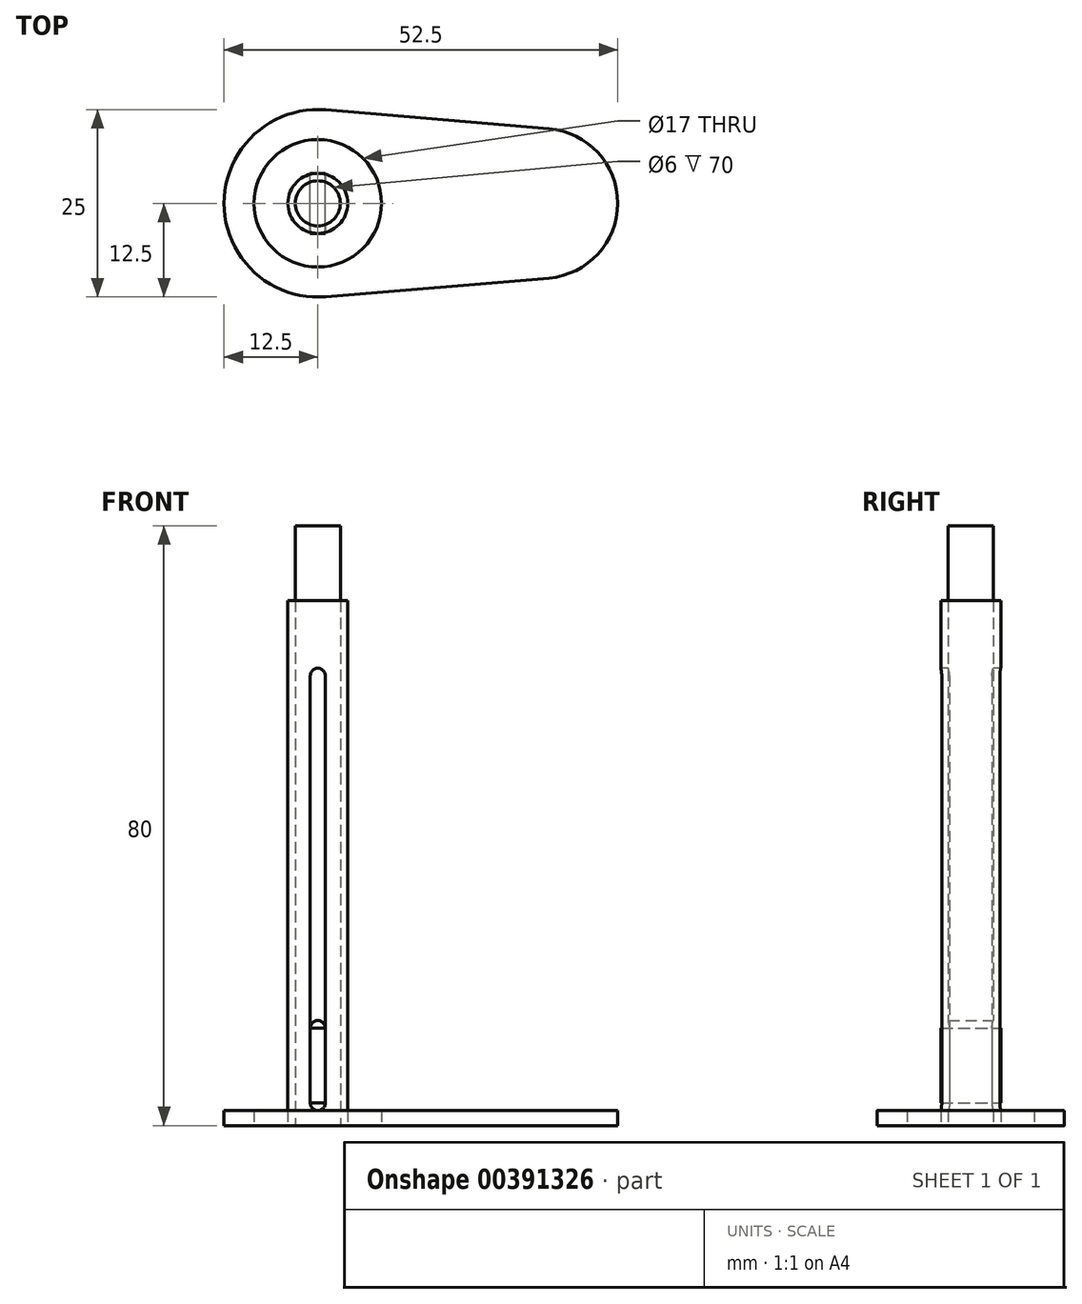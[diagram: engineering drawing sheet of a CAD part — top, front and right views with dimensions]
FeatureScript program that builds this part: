
annotation { "Feature Type Name" : "Feature", "Feature Type Description" : "" }
export const myFeature = defineFeature(function(context is Context, id is Id, definition is map)
    precondition{}
    {
        {
            var Q0;
            Q0=qCreatedBy(makeId("Top.planeOp"),FACE);
            var sketch = newSketch(context, id + "F0", { "sketchPlane" : qUnion([Q0])});
            skCircle(sketch, "E0", {"center": v(0, 0) * mm, "radius": 4 * mm});
            skCircle(sketch, "E1", {"center": v(0, 0) * mm, "radius": 3 * mm});
            skSolve(sketch);
        }
        {
            var Q0;
            Q0=makeQuery(id+"F0.imprint","IMPRINT",FACE,{"disambiguationData":[TD([[makeQuery(id+"F0.imprint","IMPRINT",EDGE,{"derivedFrom":sQuery(id+"F0.wireOp",EDGE,"E0")}),1.0]])]});
            extrude(context, id + "F1", {"entities" : qUnion([Q0]), "depth" : 70 * mm});
        }
        {
            var Q0;
            Q0=qCreatedBy(makeId("Front.planeOp"),FACE);
            var sketch = newSketch(context, id + "F2", { "sketchPlane" : qUnion([Q0])});
            skLineSegment(sketch, "E2", {"start": v(-4, 0) * mm, "end": v(-4, 70) * mm});
            skLineSegment(sketch, "E3", {"start": v(4, 70) * mm, "end": v(4, 0) * mm});
            skLineSegment(sketch, "E4.0", {"start": v(-4, 70) * mm, "end": v(4, 70) * mm});
            skLineSegment(sketch, "E5", {"start": v(-1, 60) * mm, "end": v(-1, 10) * mm});
            skLineSegment(sketch, "E6", {"start": v(1, 60) * mm, "end": v(1, 10) * mm});
            skArc(sketch, "E7", {"start": v(1, 60) * mm, "mid": v(0, 61) * mm, "end": v(-1, 60) * mm});
            skArc(sketch, "E8", {"start": v(-1, 10) * mm, "mid": v(0, 9) * mm, "end": v(1, 10) * mm});
            skSolve(sketch);
        }
        {
            var Q0;
            Q0=qSketchRegion(id+"F2",true);
            extrude(context, id + "F3", {"entities" : qUnion([Q0]), "operationType" : NewBodyOperationType.REMOVE, "endBound" : BoundingType.SYMMETRIC, "oppositeDirection" : true, "depth" : 25 * mm});
        }
        {
            var Q0;
            Q0=qCreatedBy(makeId("Top.planeOp"),FACE);
            var sketch = newSketch(context, id + "F4", { "sketchPlane" : qUnion([Q0])});
            skCircle(sketch, "E9", {"center": v(0, 0) * mm, "radius": 3 * mm});
            skSolve(sketch);
        }
        {
            var Q0;
            Q0=makeQuery(id+"F4.imprint","IMPRINT",FACE,{"disambiguationData":[TD([[makeQuery(id+"F4.imprint","IMPRINT",EDGE,{"derivedFrom":sQuery(id+"F4.wireOp",EDGE,"E9")}),1.0]])]});
            extrude(context, id + "F5", {"entities" : qUnion([Q0]), "depth" : 80 * mm});
        }
        {
            var Q0;
            Q0=qCreatedBy(makeId("Front.planeOp"),FACE);
            var sketch = newSketch(context, id + "F6", { "sketchPlane" : qUnion([Q0])});
            skLineSegment(sketch, "E10.bottom", {"start": v(-1, 13) * mm, "end": v(1, 13) * mm});
            skLineSegment(sketch, "E10.top", {"start": v(-1, 3) * mm, "end": v(1, 3) * mm});
            skLineSegment(sketch, "E10.left", {"start": v(-1, 13) * mm, "end": v(-1, 3) * mm});
            skLineSegment(sketch, "E10.right", {"start": v(1, 13) * mm, "end": v(1, 3) * mm});
            skLineSegment(sketch, "E11", {"start": v(-3, 0) * mm, "end": v(-3, 80) * mm});
            skSolve(sketch);
        }
        {
            var Q0;
            Q0=qCreatedBy(makeId("Front.planeOp"),FACE);
            var sketch = newSketch(context, id + "F7", { "sketchPlane" : qUnion([Q0])});
            skLineSegment(sketch, "E12.left", {"start": v(-1, 13) * mm, "end": v(-1, 3) * mm});
            skLineSegment(sketch, "E12.right", {"start": v(1, 13) * mm, "end": v(1, 3) * mm});
            skLineSegment(sketch, "E13", {"start": v(-3, 0) * mm, "end": v(-3, 80) * mm});
            skArc(sketch, "E14", {"start": v(1, 13) * mm, "mid": v(0, 14) * mm, "end": v(-1, 13) * mm});
            skArc(sketch, "E15", {"start": v(-1, 3) * mm, "mid": v(0, 2) * mm, "end": v(1, 3) * mm});
            skSolve(sketch);
        }
        {
            var Q0;
            Q0=qSketchRegion(id+"F7",true);
            extrude(context, id + "F8", {"entities" : qUnion([Q0]), "operationType" : NewBodyOperationType.REMOVE, "endBound" : BoundingType.SYMMETRIC, "depth" : 25 * mm});
        }
        {
            var Q0;
            Q0=qSketchRegion(id+"F6",true);
            extrude(context, id + "F9", {"entities" : qUnion([Q0]), "endBound" : BoundingType.SYMMETRIC, "depth" : 8 * mm});
        }
        {
            var Q0;
            Q0=qCreatedBy(makeId("Top.planeOp"),FACE);
            var sketch = newSketch(context, id + "F10", { "sketchPlane" : qUnion([Q0])});
            skCircle(sketch, "E16", {"center": v(0, 0) * mm, "radius": 8.5 * mm});
            skCircle(sketch, "E17", {"center": v(0, 0) * mm, "radius": 12.5 * mm});
            skCircle(sketch, "E18", {"center": v(30, 0) * mm, "radius": 10 * mm});
            skLineSegment(sketch, "E19", {"start": v(1.04, 12.46) * mm, "end": v(30.83, 9.97) * mm});
            skLineSegment(sketch, "E20", {"start": v(1.04, -12.46) * mm, "end": v(30.83, -9.97) * mm});
            skSolve(sketch);
        }
        {
            var Q0;
            {var subQ0=sQuery(id+"F10.wireOp",EDGE,"E18");var subQ1=makeQuery(id+"F10.imprint","INTERSECT",VERTEX,{"derivedFrom":[subQ0,sQuery(id+"F10.wireOp",EDGE,"E19")]});Q0=makeQuery(id+"F10.imprint","IMPRINT",FACE,{"disambiguationData":[TD([[makeQuery(id+"F10.imprint","IMPRINT",EDGE,{"disambiguationData":[TD([[subQ1,-1.0]])],"derivedFrom":subQ0}),1.0]])]});}
            var Q1;
            {var subQ0=sQuery(id+"F10.wireOp",EDGE,"E19");Q1=makeQuery(id+"F10.imprint","IMPRINT",FACE,{"disambiguationData":[TD([[makeQuery(id+"F10.imprint","IMPRINT",EDGE,{"derivedFrom":subQ0}),-1.0]])]});}
            var Q2;
            Q2=makeQuery(id+"F10.imprint","IMPRINT",FACE,{"disambiguationData":[TD([[makeQuery(id+"F10.imprint","IMPRINT",EDGE,{"derivedFrom":sQuery(id+"F10.wireOp",EDGE,"E16")}),-1.0]])]});
            extrude(context, id + "F11", {"entities" : qUnion([Q0, Q1, Q2]), "depth" : 2 * mm});
        }
    });
